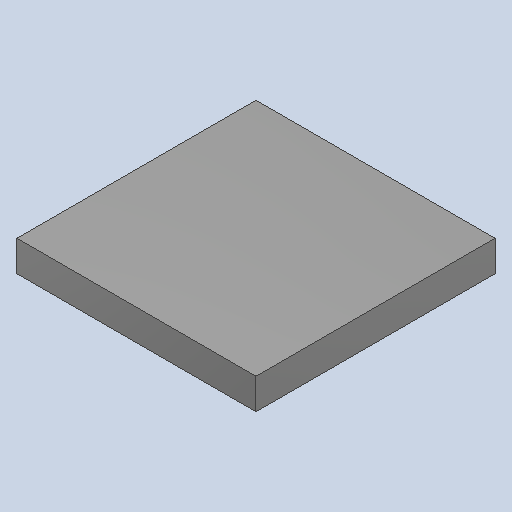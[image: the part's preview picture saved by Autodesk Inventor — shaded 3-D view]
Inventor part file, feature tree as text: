
AUTODESK INVENTOR PART (.ipt)
format: ipt  version: 2022.1 (Build 261234000, 234)  size: 82,944 bytes
history: imported  units: mm
features: imported_body x1
ambient origin geometry x8: Origin, YZ Plane, XZ Plane, XY Plane, X Axis, Y Axis, Z Axis, Center Point
bodies: Solid1 (imported_parasolid)
feature tree (1):
  imported_body  NMx_Import_Brep_tag  [imported B-rep: ~6 faces, bbox_mm=[7.0, 0.9, 7.0]]
